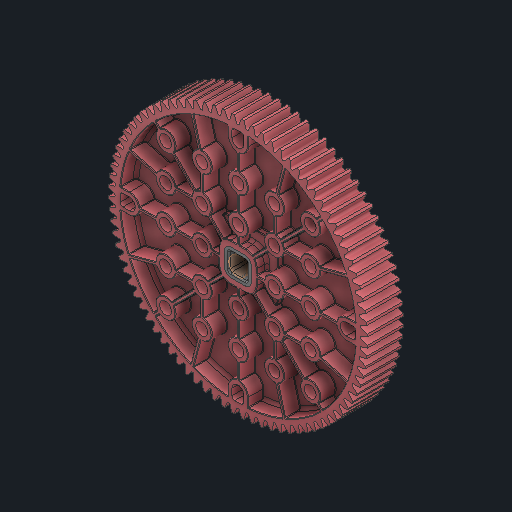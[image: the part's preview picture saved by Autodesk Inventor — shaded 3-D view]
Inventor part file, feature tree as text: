
AUTODESK INVENTOR PART (.ipt)
format: ipt  version: 2024 (Build 280153000, 153)  size: 8,411,648 bytes
history: native  units: in
note: dims shown in document units (in); Inventor stores cm internally (conversion verified against a paired STEP export)
features: other x6, sketch x1
ambient origin geometry x8: Origin, YZ Plane, XZ Plane, XY Plane, X Axis, Y Axis, Z Axis, Center Point
bodies: Solid1 (feature_tree), Solid2 (feature_tree)
feature tree (7):
  other  "HS 84T Gear, No Insert.ipt"
  other  "Solid1::HS 84T Gear, No Insert.ipt"
  other  "Solid2::HS 84T Gear, No Insert.ipt"
  other  "TaggingFeature1"
  sketch  "Sketch1"  dims[d0=0.3937in]
  other  "Srf1"
  other  "Srf1::Derived"
